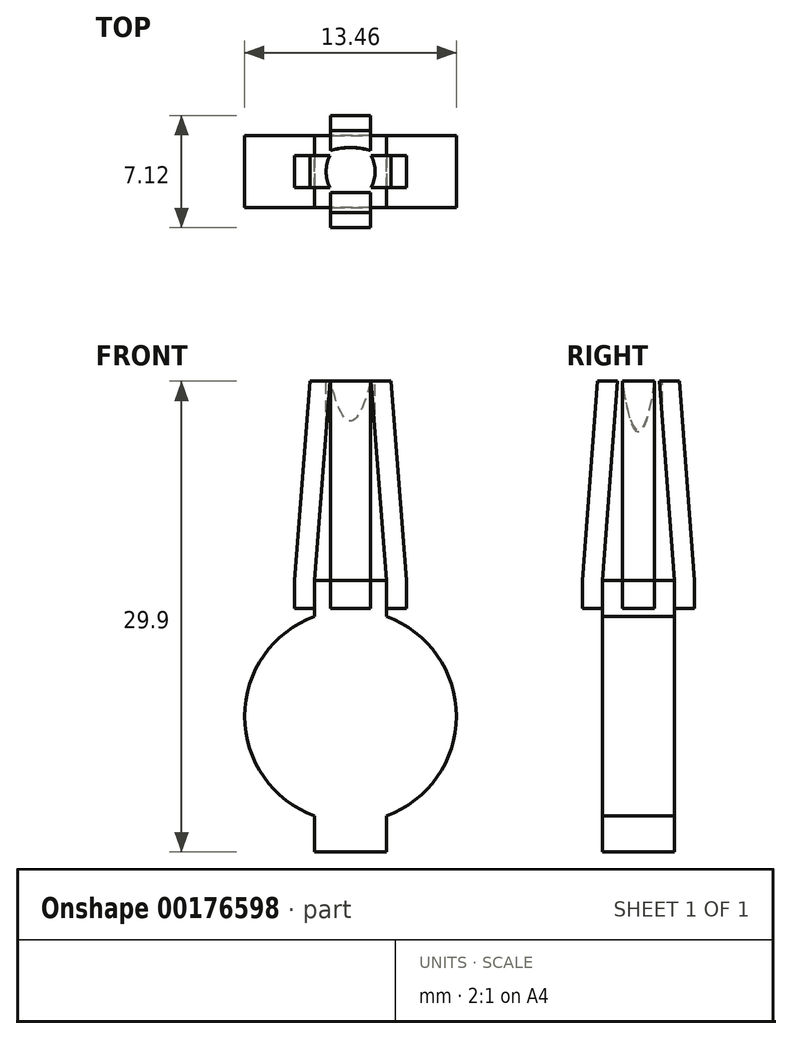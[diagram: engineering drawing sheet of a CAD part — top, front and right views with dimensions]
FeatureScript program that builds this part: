
annotation { "Feature Type Name" : "Feature", "Feature Type Description" : "" }
export const myFeature = defineFeature(function(context is Context, id is Id, definition is map)
    precondition{}
    {
        {
            var Q0;
            Q0=qCreatedBy(makeId("Front.planeOp"),FACE);
            var sketch = newSketch(context, id + "F0", { "sketchPlane" : qUnion([Q0])});
            skCircle(sketch, "E0", {"center": v(0, 0) * mm, "radius": 6.73 * mm});
            skLineSegment(sketch, "E1", {"start": v(0, 0) * mm, "end": v(-2.28, 0) * mm});
            skLineSegment(sketch, "E2", {"start": v(-2.28, 0) * mm, "end": v(-2.28, 6.33) * mm});
            skLineSegment(sketch, "E3", {"start": v(0, 0) * mm, "end": v(2.29, 0) * mm});
            skLineSegment(sketch, "E4", {"start": v(2.29, 0) * mm, "end": v(2.29, 6.33) * mm});
            skLineSegment(sketch, "E5", {"start": v(2.29, 6.33) * mm, "end": v(2.29, 6.84) * mm});
            skLineSegment(sketch, "E6", {"start": v(2.29, 6.84) * mm, "end": v(-2.28, 6.84) * mm});
            skLineSegment(sketch, "E7", {"start": v(-2.28, 6.84) * mm, "end": v(-2.28, 6.33) * mm});
            skLineSegment(sketch, "E8", {"start": v(-2.28, 0) * mm, "end": v(-2.28, -6.33) * mm});
            skLineSegment(sketch, "E9", {"start": v(2.29, 0) * mm, "end": v(2.29, -6.33) * mm});
            skLineSegment(sketch, "E10", {"start": v(2.29, -6.33) * mm, "end": v(2.29, -6.84) * mm});
            skLineSegment(sketch, "E11", {"start": v(2.29, -6.84) * mm, "end": v(-2.28, -6.84) * mm});
            skLineSegment(sketch, "E12", {"start": v(-2.28, -6.84) * mm, "end": v(-2.28, -6.33) * mm});
            skLineSegment(sketch, "E13", {"start": v(-2.28, -6.84) * mm, "end": v(-2.28, -7.86) * mm});
            skLineSegment(sketch, "E14", {"start": v(-2.28, -7.86) * mm, "end": v(2.29, -7.86) * mm});
            skLineSegment(sketch, "E15", {"start": v(2.29, -7.86) * mm, "end": v(2.29, -6.84) * mm});
            skLineSegment(sketch, "E16", {"start": v(-2.28, 6.84) * mm, "end": v(-2.28, 7.86) * mm});
            skLineSegment(sketch, "E17", {"start": v(-2.28, 7.86) * mm, "end": v(2.29, 7.86) * mm});
            skLineSegment(sketch, "E18", {"start": v(2.29, 7.86) * mm, "end": v(2.29, 6.84) * mm});
            skLineSegment(sketch, "E19", {"start": v(-2.28, -7.86) * mm, "end": v(-2.28, -8.62) * mm});
            skLineSegment(sketch, "E20", {"start": v(-2.28, -8.62) * mm, "end": v(2.29, -8.62) * mm});
            skLineSegment(sketch, "E21", {"start": v(2.29, -8.62) * mm, "end": v(2.29, -7.86) * mm});
            skLineSegment(sketch, "E22", {"start": v(2.29, 7.86) * mm, "end": v(2.29, 8.62) * mm});
            skLineSegment(sketch, "E23", {"start": v(2.29, 8.62) * mm, "end": v(-2.28, 8.62) * mm});
            skLineSegment(sketch, "E24", {"start": v(-2.28, 8.62) * mm, "end": v(-2.28, 7.86) * mm});
            skSolve(sketch);
        }
        {
            var Q0;
            Q0 = qSketchRegion(id + "F0", true);
            extrude(context, id + "F1", {"entities" : qUnion([Q0]), "depth" : 4.57 * mm});
        }
        {
            var Q0;
            Q0=qCreatedBy(makeId("Right.planeOp"),FACE);
            var sketch = newSketch(context, id + "F2", { "sketchPlane" : qUnion([Q0])});
            skLineSegment(sketch, "E25", {"start": v(0, 8.62) * mm, "end": v(0, 6.85) * mm});
            skLineSegment(sketch, "E26", {"start": v(0, 6.85) * mm, "end": v(1.27, 6.85) * mm});
            skLineSegment(sketch, "E27", {"start": v(1.27, 6.85) * mm, "end": v(1.27, 8.62) * mm});
            skLineSegment(sketch, "E28", {"start": v(1.27, 8.62) * mm, "end": v(0, 8.62) * mm});
            skLineSegment(sketch, "E29", {"start": v(-4.57, 8.62) * mm, "end": v(-5.85, 8.62) * mm});
            skLineSegment(sketch, "E30", {"start": v(-5.85, 8.62) * mm, "end": v(-5.85, 6.85) * mm});
            skLineSegment(sketch, "E31", {"start": v(-5.85, 6.85) * mm, "end": v(-4.57, 6.85) * mm});
            skLineSegment(sketch, "E32", {"start": v(-4.57, 6.85) * mm, "end": v(-4.57, 8.62) * mm});
            skLineSegment(sketch, "E33", {"start": v(1.27, 8.62) * mm, "end": v(0.31, 8.62) * mm});
            skLineSegment(sketch, "E34", {"start": v(1.27, 8.62) * mm, "end": v(0.31, 21.28) * mm});
            skLineSegment(sketch, "E35", {"start": v(0.31, 21.28) * mm, "end": v(-0.95, 21.28) * mm});
            skLineSegment(sketch, "E36", {"start": v(-0.95, 21.28) * mm, "end": v(0, 8.62) * mm});
            skLineSegment(sketch, "E37", {"start": v(-5.85, 8.62) * mm, "end": v(-4.9, 8.62) * mm});
            skLineSegment(sketch, "E38", {"start": v(-5.85, 8.62) * mm, "end": v(-4.9, 21.28) * mm});
            skLineSegment(sketch, "E39", {"start": v(-4.9, 21.28) * mm, "end": v(-3.62, 21.28) * mm});
            skLineSegment(sketch, "E40", {"start": v(-3.62, 21.28) * mm, "end": v(-4.57, 8.62) * mm});
            skSolve(sketch);
        }
        {
            var Q0;
            Q0 = qSketchRegion(id + "F2", true);
            extrude(context, id + "F3", {"entities" : qUnion([Q0]), "operationType" : NewBodyOperationType.ADD, "depth" : 1.27 * mm});
        }
        {
            var Q0;
            Q0=makeQuery(id+"F3.opExtrude","CAP_FACE",FACE,{"disambiguationData":[OSD([sQuery(id+"F2.wireOp",EDGE,"E25"),sQuery(id+"F2.wireOp",EDGE,"E26"),sQuery(id+"F2.wireOp",EDGE,"E27"),sQuery(id+"F2.wireOp",EDGE,"E34"),sQuery(id+"F2.wireOp",EDGE,"E35"),sQuery(id+"F2.wireOp",EDGE,"E36")])],"isStart":true});
            var Q1;
            Q1=makeQuery(id+"F3.opExtrude","CAP_FACE",FACE,{"disambiguationData":[OSD([sQuery(id+"F2.wireOp",EDGE,"E30"),sQuery(id+"F2.wireOp",EDGE,"E31"),sQuery(id+"F2.wireOp",EDGE,"E32"),sQuery(id+"F2.wireOp",EDGE,"E38"),sQuery(id+"F2.wireOp",EDGE,"E39"),sQuery(id+"F2.wireOp",EDGE,"E40")])],"isStart":true});
            extrude(context, id + "F4", {"entities" : qUnion([Q0, Q1]), "operationType" : NewBodyOperationType.ADD, "depth" : 1.27 * mm});
        }
        {
            var Q0;
            Q0=makeQuery(id+"F1.opExtrude","CAP_FACE",FACE,{"disambiguationData":[OSD([sQuery(id+"F0.wireOp",EDGE,"E0"),sQuery(id+"F0.wireOp",EDGE,"E5"),sQuery(id+"F0.wireOp",EDGE,"E7"),sQuery(id+"F0.wireOp",EDGE,"E10"),sQuery(id+"F0.wireOp",EDGE,"E12"),sQuery(id+"F0.wireOp",EDGE,"E13"),sQuery(id+"F0.wireOp",EDGE,"E15"),sQuery(id+"F0.wireOp",EDGE,"E16"),sQuery(id+"F0.wireOp",EDGE,"E18"),sQuery(id+"F0.wireOp",EDGE,"E19"),sQuery(id+"F0.wireOp",EDGE,"E20"),sQuery(id+"F0.wireOp",EDGE,"E21"),sQuery(id+"F0.wireOp",EDGE,"E22"),sQuery(id+"F0.wireOp",EDGE,"E23"),sQuery(id+"F0.wireOp",EDGE,"E24")])],"isStart":false});
            var sketch = newSketch(context, id + "F5", { "sketchPlane" : qUnion([Q0])});
            skLineSegment(sketch, "E41", {"start": v(-2.28, 8.62) * mm, "end": v(-3.55, 8.62) * mm});
            skLineSegment(sketch, "E42", {"start": v(-3.55, 8.62) * mm, "end": v(-3.55, 6.85) * mm});
            skLineSegment(sketch, "E43", {"start": v(-3.55, 6.85) * mm, "end": v(-2.28, 6.85) * mm});
            skLineSegment(sketch, "E44", {"start": v(-2.28, 6.85) * mm, "end": v(-2.28, 8.62) * mm});
            skLineSegment(sketch, "E45", {"start": v(-3.55, 8.62) * mm, "end": v(-2.58, 8.62) * mm});
            skLineSegment(sketch, "E46", {"start": v(2.29, 8.62) * mm, "end": v(2.29, 6.85) * mm});
            skLineSegment(sketch, "E47", {"start": v(2.29, 6.85) * mm, "end": v(3.56, 6.85) * mm});
            skLineSegment(sketch, "E48", {"start": v(3.56, 6.85) * mm, "end": v(3.56, 8.62) * mm});
            skLineSegment(sketch, "E49", {"start": v(3.56, 8.62) * mm, "end": v(2.29, 8.62) * mm});
            skLineSegment(sketch, "E50", {"start": v(3.56, 8.62) * mm, "end": v(2.59, 8.62) * mm});
            skLineSegment(sketch, "E51", {"start": v(-3.55, 8.62) * mm, "end": v(-2.58, 21.28) * mm});
            skLineSegment(sketch, "E52", {"start": v(-2.58, 21.28) * mm, "end": v(-1.31, 21.28) * mm});
            skLineSegment(sketch, "E53", {"start": v(-1.31, 21.28) * mm, "end": v(-2.28, 8.62) * mm});
            skLineSegment(sketch, "E54", {"start": v(3.56, 8.62) * mm, "end": v(2.59, 21.28) * mm});
            skLineSegment(sketch, "E55", {"start": v(2.59, 21.28) * mm, "end": v(1.31, 21.28) * mm});
            skLineSegment(sketch, "E56", {"start": v(1.31, 21.28) * mm, "end": v(2.29, 8.62) * mm});
            skSolve(sketch);
        }
        {
            var Q0;
            Q0 = qSketchRegion(id + "F5", true);
            extrude(context, id + "F6", {"entities" : qUnion([Q0]), "operationType" : NewBodyOperationType.ADD, "oppositeDirection" : true, "depth" : 3.3 * mm});
        }
        {
            var Q0;
            Q0=makeQuery(id+"F6.boolean.opBoolean","MERGE",FACE,{"derivedFrom":[makeQuery(id+"F1.opExtrude","CAP_FACE",FACE,{"disambiguationData":[OSD([sQuery(id+"F0.wireOp",EDGE,"E0"),sQuery(id+"F0.wireOp",EDGE,"E5"),sQuery(id+"F0.wireOp",EDGE,"E7"),sQuery(id+"F0.wireOp",EDGE,"E10"),sQuery(id+"F0.wireOp",EDGE,"E12"),sQuery(id+"F0.wireOp",EDGE,"E13"),sQuery(id+"F0.wireOp",EDGE,"E15"),sQuery(id+"F0.wireOp",EDGE,"E16"),sQuery(id+"F0.wireOp",EDGE,"E18"),sQuery(id+"F0.wireOp",EDGE,"E19"),sQuery(id+"F0.wireOp",EDGE,"E20"),sQuery(id+"F0.wireOp",EDGE,"E21"),sQuery(id+"F0.wireOp",EDGE,"E22"),sQuery(id+"F0.wireOp",EDGE,"E23"),sQuery(id+"F0.wireOp",EDGE,"E24")])],"isStart":false}),makeQuery(id+"F6.opExtrude","CAP_FACE",FACE,{"disambiguationData":[OSD([sQuery(id+"F5.wireOp",EDGE,"E42"),sQuery(id+"F5.wireOp",EDGE,"E43"),sQuery(id+"F5.wireOp",EDGE,"E44"),sQuery(id+"F5.wireOp",EDGE,"E51"),sQuery(id+"F5.wireOp",EDGE,"E52"),sQuery(id+"F5.wireOp",EDGE,"E53")])],"isStart":true}),makeQuery(id+"F6.opExtrude","CAP_FACE",FACE,{"disambiguationData":[OSD([sQuery(id+"F5.wireOp",EDGE,"E46"),sQuery(id+"F5.wireOp",EDGE,"E47"),sQuery(id+"F5.wireOp",EDGE,"E48"),sQuery(id+"F5.wireOp",EDGE,"E54"),sQuery(id+"F5.wireOp",EDGE,"E55"),sQuery(id+"F5.wireOp",EDGE,"E56")])],"isStart":true})]});
            var sketch = newSketch(context, id + "F7", { "sketchPlane" : qUnion([Q0])});
            skLineSegment(sketch, "E57", {"start": v(-2.28, 8.62) * mm, "end": v(-2.28, 6.85) * mm});
            skLineSegment(sketch, "E58", {"start": v(2.29, 6.85) * mm, "end": v(2.29, 8.62) * mm});
            skSolve(sketch);
        }
        {
            var Q0;
            Q0 = qSketchRegion(id + "F7", true);
            var Q1;
            Q1=makeQuery(id+"F7.imprint","IMPRINT",FACE,{"disambiguationData":[TD([[makeQuery(id+"F7.imprint","IMPRINT",EDGE,{"derivedFrom":sQuery(id+"F7.wireOp",EDGE,"E57")}),-1.0]])]});
            var Q2;
            Q2=makeQuery(id+"F7.imprint","IMPRINT",FACE,{"disambiguationData":[TD([[makeQuery(id+"F7.imprint","IMPRINT",EDGE,{"derivedFrom":sQuery(id+"F7.wireOp",EDGE,"E58")}),-1.0]])]});
            extrude(context, id + "F8", {"entities" : qUnion([Q0, Q1, Q2]), "operationType" : NewBodyOperationType.REMOVE, "oppositeDirection" : true, "depth" : 1.27 * mm});
        }
        {
            var Q0;
            Q0=makeQuery(id+"F6.opExtrude","SWEPT_FACE",FACE,{"disambiguationData":[OSD([sQuery(id+"F5.wireOp",EDGE,"E52")])]});
            var sketch = newSketch(context, id + "F9", { "sketchPlane" : qUnion([Q0])});
            skArc(sketch, "E59", {"start": v(-1.31, -1.27) * mm, "mid": v(-1.55, -2.29) * mm, "end": v(-1.31, -3.3) * mm});
            skLineSegment(sketch, "E60", {"start": v(-1.31, -1.27) * mm, "end": v(-1.31, -3.3) * mm});
            skSolve(sketch);
        }
        {
            var Q0;
            Q0=makeQuery(id+"F9.imprint","IMPRINT",FACE,{"disambiguationData":[TD([[makeQuery(id+"F9.imprint","IMPRINT",EDGE,{"derivedFrom":sQuery(id+"F9.wireOp",EDGE,"E59")}),1.0]])]});
            extrude(context, id + "F10", {"entities" : qUnion([Q0]), "operationType" : NewBodyOperationType.REMOVE, "oppositeDirection" : true, "depth" : 10.16 * mm});
        }
        {
            var Q0;
            {var subQ0=sQuery(id+"F2.wireOp",EDGE,"E35");Q0=makeQuery(id+"F4.boolean.opBoolean","MERGE",FACE,{"derivedFrom":[makeQuery(id+"F3.opExtrude","SWEPT_FACE",FACE,{"disambiguationData":[OSD([subQ0])]}),makeQuery(id+"F4.opExtrude","SWEPT_FACE",FACE,{"disambiguationData":[OSD([subQ0])]})]});}
            var sketch = newSketch(context, id + "F11", { "sketchPlane" : qUnion([Q0])});
            skArc(sketch, "E61", {"start": v(1.27, -0.97) * mm, "mid": v(0, -0.78) * mm, "end": v(-1.27, -0.97) * mm});
            skSolve(sketch);
        }
        {
            var Q0;
            Q0=makeQuery(id+"F11.imprint","IMPRINT",FACE,{"disambiguationData":[TD([[makeQuery(id+"F11.imprint","IMPRINT",EDGE,{"derivedFrom":sQuery(id+"F11.wireOp",EDGE,"E61")}),1.0]])]});
            extrude(context, id + "F12", {"entities" : qUnion([Q0]), "operationType" : NewBodyOperationType.REMOVE, "oppositeDirection" : true, "depth" : 10.16 * mm});
        }
        {
            var Q0;
            Q0=makeQuery(id+"F6.opExtrude","SWEPT_FACE",FACE,{"disambiguationData":[OSD([sQuery(id+"F5.wireOp",EDGE,"E55")])]});
            var sketch = newSketch(context, id + "F13", { "sketchPlane" : qUnion([Q0])});
            skArc(sketch, "E62", {"start": v(1.31, -3.3) * mm, "mid": v(1.56, -2.29) * mm, "end": v(1.31, -1.27) * mm});
            skSolve(sketch);
        }
        {
            var Q0;
            Q0=makeQuery(id+"F13.imprint","IMPRINT",FACE,{"disambiguationData":[TD([[makeQuery(id+"F13.imprint","IMPRINT",EDGE,{"derivedFrom":sQuery(id+"F13.wireOp",EDGE,"E62")}),1.0]])]});
            extrude(context, id + "F14", {"entities" : qUnion([Q0]), "operationType" : NewBodyOperationType.REMOVE, "oppositeDirection" : true, "depth" : 10.16 * mm});
        }
        {
            var Q0;
            Q0=makeQuery(id+"F4.opExtrude","SWEPT_FACE",FACE,{"disambiguationData":[OSD([sQuery(id+"F2.wireOp",EDGE,"E39")])]});
            var sketch = newSketch(context, id + "F15", { "sketchPlane" : qUnion([Q0])});
            skArc(sketch, "E63", {"start": v(-1.27, -3.62) * mm, "mid": v(0, -3.83) * mm, "end": v(1.27, -3.62) * mm});
            skLineSegment(sketch, "E64", {"start": v(-1.27, -3.62) * mm, "end": v(1.27, -3.62) * mm});
            skSolve(sketch);
        }
        {
            var Q0;
            {var subQ0=sQuery(id+"F15.wireOp",EDGE,"E64");var subQ1=sQuery(id+"F15.wireOp",EDGE,"E63");var subQ2=makeQuery(id+"F15.imprint","INTERSECT",VERTEX,{"derivedFrom":[subQ1,subQ0]});Q0=makeQuery(id+"F15.imprint","IMPRINT",FACE,{"disambiguationData":[TD([[makeQuery(id+"F15.imprint","IMPRINT",EDGE,{"disambiguationData":[TD([[subQ2,1.0]])],"derivedFrom":subQ1}),1.0]])]});}
            var Q1;
            {var subQ0=sQuery(id+"F15.wireOp",EDGE,"E64");var subQ2=sQuery(id+"F2.wireOp",EDGE,"E39");var subQ4=makeQuery(id+"F4.opExtrude","CAP_EDGE",EDGE,{"disambiguationData":[OSD([subQ2])],"isStart":true});var subQ6=makeQuery(id+"F15.imprint","INTERSECT",VERTEX,{"derivedFrom":[subQ4,subQ0]});Q1=makeQuery(id+"F15.imprint","IMPRINT",FACE,{"disambiguationData":[TD([[makeQuery(id+"F15.imprint","IMPRINT",EDGE,{"disambiguationData":[TD([[subQ6,1.0]])],"derivedFrom":subQ4}),1.0]])]});}
            extrude(context, id + "F16", {"entities" : qUnion([Q0, Q1]), "operationType" : NewBodyOperationType.REMOVE, "oppositeDirection" : true, "depth" : 10.16 * mm});
        }
    });
